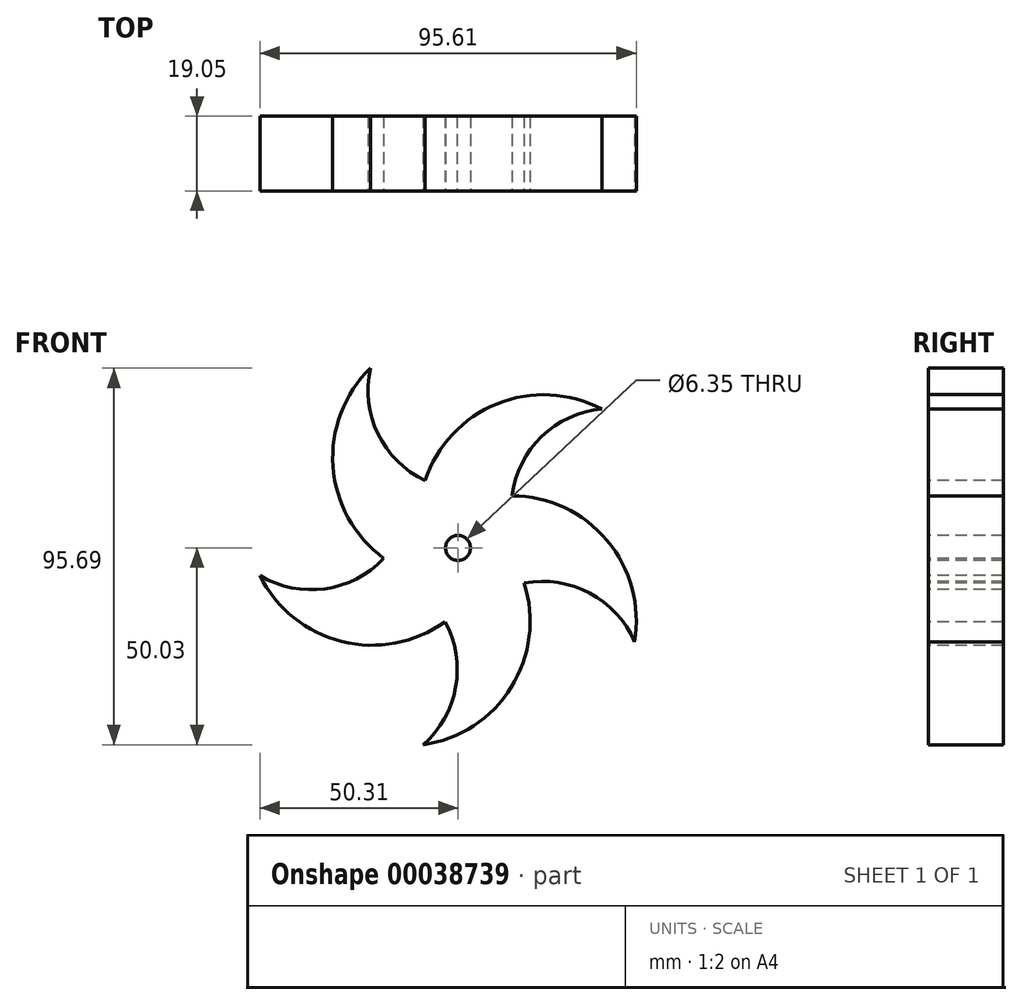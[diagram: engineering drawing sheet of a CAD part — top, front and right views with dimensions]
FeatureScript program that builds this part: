
annotation { "Feature Type Name" : "Feature", "Feature Type Description" : "" }
export const myFeature = defineFeature(function(context is Context, id is Id, definition is map)
    precondition{}
    {
        {
            var Q0;
            Q0=qCreatedBy(makeId("Front.planeOp"),FACE);
            var sketch = newSketch(context, id + "F0", { "sketchPlane" : qUnion([Q0])});
            skArc(sketch, "E0", {"start": v(44.85, -23.86) * mm, "mid": v(37.87, 1.9) * mm, "end": v(13.7, 13.23) * mm});
            skArc(sketch, "E1", {"start": v(-8.84, -50.03) * mm, "mid": v(13.5, -35.43) * mm, "end": v(16.82, -8.95) * mm});
            skArc(sketch, "E2", {"start": v(-50.3, -7.06) * mm, "mid": v(-29.52, -23.79) * mm, "end": v(-3.31, -18.76) * mm});
            skArc(sketch, "E3", {"start": v(-22.26, 45.66) * mm, "mid": v(-31.75, 20.72) * mm, "end": v(-18.87, -2.65) * mm});
            skArc(sketch, "E4", {"start": v(36.55, 35.28) * mm, "mid": v(9.9, 36.6) * mm, "end": v(-8.35, 17.12) * mm});
            skArc(sketch, "E5", {"start": v(-22.26, 45.66) * mm, "mid": v(-20.31, 28.95) * mm, "end": v(-8.35, 17.12) * mm});
            skArc(sketch, "E6", {"start": v(36.55, 35.28) * mm, "mid": v(21.26, 28.26) * mm, "end": v(13.7, 13.23) * mm});
            skArc(sketch, "E7", {"start": v(44.85, -23.86) * mm, "mid": v(33.45, -11.49) * mm, "end": v(16.82, -8.95) * mm});
            skArc(sketch, "E8", {"start": v(-8.84, -50.03) * mm, "mid": v(-0.59, -35.36) * mm, "end": v(-3.31, -18.76) * mm});
            skArc(sketch, "E9", {"start": v(-50.3, -7.06) * mm, "mid": v(-33.81, -10.37) * mm, "end": v(-18.87, -2.65) * mm});
            skCircle(sketch, "E10", {"center": v(0, 0) * mm, "radius": 3.18 * mm});
            skSolve(sketch);
        }
        {
            var Q0;
            Q0=makeQuery(id+"F0.imprint","IMPRINT",FACE,{"disambiguationData":[TD([[makeQuery(id+"F0.imprint","IMPRINT",EDGE,{"derivedFrom":sQuery(id+"F0.wireOp",EDGE,"E0")}),1.0]])]});
            extrude(context, id + "F1", {"entities" : qUnion([Q0]), "oppositeDirection" : true, "depth" : 19.05 * mm});
        }
    });
